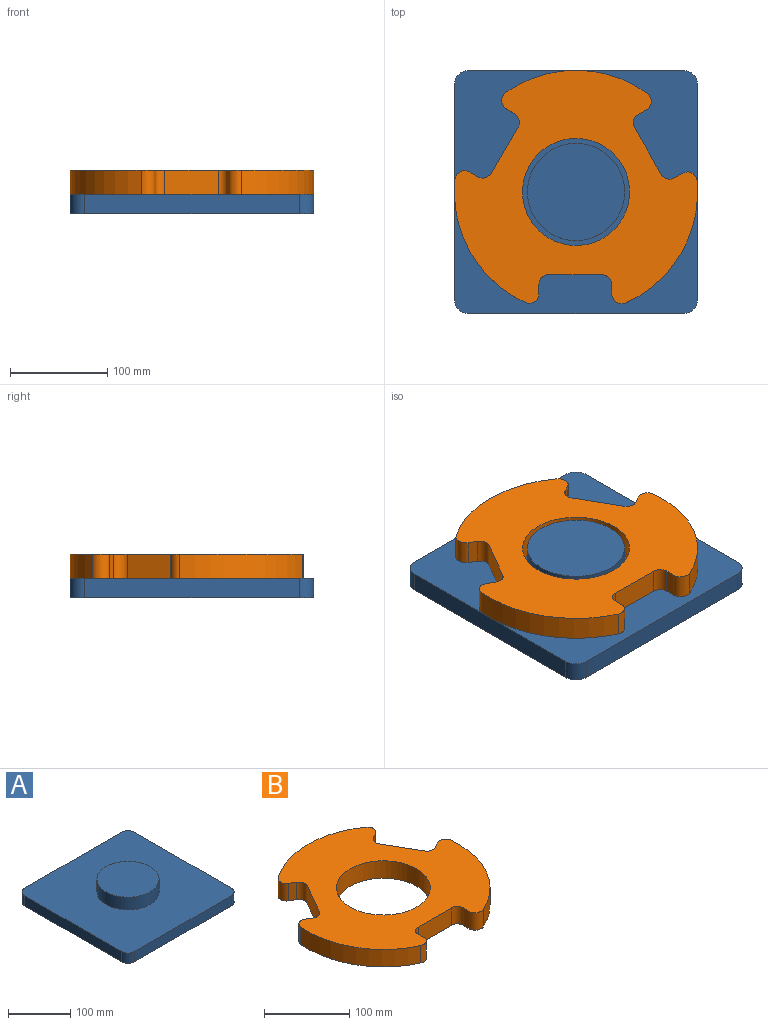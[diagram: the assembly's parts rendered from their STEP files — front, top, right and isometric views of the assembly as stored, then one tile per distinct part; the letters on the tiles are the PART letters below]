
ASSEMBLY  parts=2 mates=1
PART A: 12 faces, bbox 250x250x45 mm
  f0: plane 220x20mm, normal (1,0,0), area 4400mm2, adj f4,f5,f8,f11
  f1: plane 220x20mm, normal (0,1,0), area 4400mm2, adj f4,f5,f8,f9
  f2: plane 220x20mm, normal (-1,0,0), area 4400mm2, adj f4,f5,f9,f10
  f3: plane 220x20mm, normal (0,-1,0), area 4400mm2, adj f4,f5,f10,f11
  f4: plane 250x250mm, normal (0,0,1), area 54452.9mm2, adj f0,f1,f2,f3,f6,f8,f9,f10
  f5: plane 250x250mm, normal (0,0,-1), area 62306.9mm2, adj f0,f1,f2,f3,f8,f9,f10,f11
  f6: cylinder r=50mm len=100mm, axis (0,0,-1), area 7854mm2, adj f4,f7
  f7: plane 100x100mm, normal (0,0,1), area 7854mm2, adj f6
  f8: cylinder r=15mm len=20mm, axis (0,0,-1), area 471.2mm2, adj f0,f1,f4,f5
  f9: cylinder r=15mm len=20mm, axis (0,0,1), area 471.2mm2, adj f1,f2,f4,f5
  f10: cylinder r=15mm len=20mm, axis (0,0,-1), area 471.2mm2, adj f2,f3,f4,f5
  f11: cylinder r=15mm len=20mm, axis (0,0,1), area 471.2mm2, adj f0,f3,f4,f5
PART B: 27 faces, bbox 250x239.7x25 mm
  f0: plane 250x239.73mm, normal (0,0,1), area 30837.4mm2, adj f2,f3,f4,f5,f6,f7,f8,f9
  f1: plane 250x239.73mm, normal (0,0,-1), area 30837.4mm2, adj f2,f3,f4,f5,f6,f7,f8,f9
  f2: cylinder r=125mm len=145.54mm, axis (0,0,-1), area 3883.8mm2, adj f0,f1,f18,f26
  f3: cylinder r=125mm len=126.05mm, axis (0,0,-1), area 3883.8mm2, adj f0,f1,f11,f19
  f4: cylinder r=55mm len=110mm, axis (0,0,-1), area 8639.4mm2, adj f0,f1
  f5: cylinder r=125mm len=126.05mm, axis (0,0,-1), area 3883.8mm2, adj f0,f1,f12,f25
  f6: plane 25x9.73mm, normal (-1,0,0), area 243.3mm2, adj f0,f1,f9,f12
  f7: plane 55x25mm, normal (0,-1,0), area 1375mm2, adj f0,f1,f9,f10
  f8: plane 25x9.73mm, normal (1,0,0), area 243.3mm2, adj f0,f1,f10,f11
  f9: cylinder r=10mm len=25mm, axis (0,0,-1), area 392.7mm2, adj f0,f1,f6,f7
  f10: cylinder r=10mm len=25mm, axis (0,0,-1), area 392.7mm2, adj f0,f1,f7,f8
  f11: cylinder r=10mm len=25mm, axis (0,0,-1), area 499.1mm2, adj f0,f1,f3,f8
  f12: cylinder r=10mm len=25mm, axis (0,0,-1), area 499.1mm2, adj f0,f1,f5,f6
  f13: plane 25x8.43mm, normal (0.5,0.87,0), area 243.3mm2, adj f0,f1,f16,f19
  f14: plane 47.63x27.5mm, normal (-0.87,0.5,0), area 1375mm2, adj f0,f1,f16,f17
  f15: plane 25x8.43mm, normal (-0.5,-0.87,0), area 243.3mm2, adj f0,f1,f17,f18
  f16: cylinder r=10mm len=25mm, axis (0,0,-1), area 392.7mm2, adj f0,f1,f13,f14
  f17: cylinder r=10mm len=25mm, axis (0,0,-1), area 392.7mm2, adj f0,f1,f14,f15
  f18: cylinder r=10mm len=25mm, axis (0,0,-1), area 499.1mm2, adj f0,f1,f2,f15
  f19: cylinder r=10mm len=25mm, axis (0,0,-1), area 499.1mm2, adj f0,f1,f3,f13
  f20: plane 25x8.43mm, normal (0.5,-0.87,0), area 243.3mm2, adj f0,f1,f23,f26
  f21: plane 47.63x27.5mm, normal (0.87,0.5,0), area 1375mm2, adj f0,f1,f23,f24
  f22: plane 25x8.43mm, normal (-0.5,0.87,0), area 243.3mm2, adj f0,f1,f24,f25
  f23: cylinder r=10mm len=25mm, axis (0,0,-1), area 392.7mm2, adj f0,f1,f20,f21
  f24: cylinder r=10mm len=25mm, axis (0,0,-1), area 392.7mm2, adj f0,f1,f21,f22
  f25: cylinder r=10mm len=25mm, axis (0,0,-1), area 499.1mm2, adj f0,f1,f5,f22
  f26: cylinder r=10mm len=25mm, axis (0,0,-1), area 499.1mm2, adj f0,f1,f2,f20
PLACE A at identity fixed
PLACE B rot(axis=(0,0,-1),120.3deg) t=(0,0,0)mm
MATE revolute A.f6 <-> B.f2  axis (0,0,1) through (0,0,45)mm
